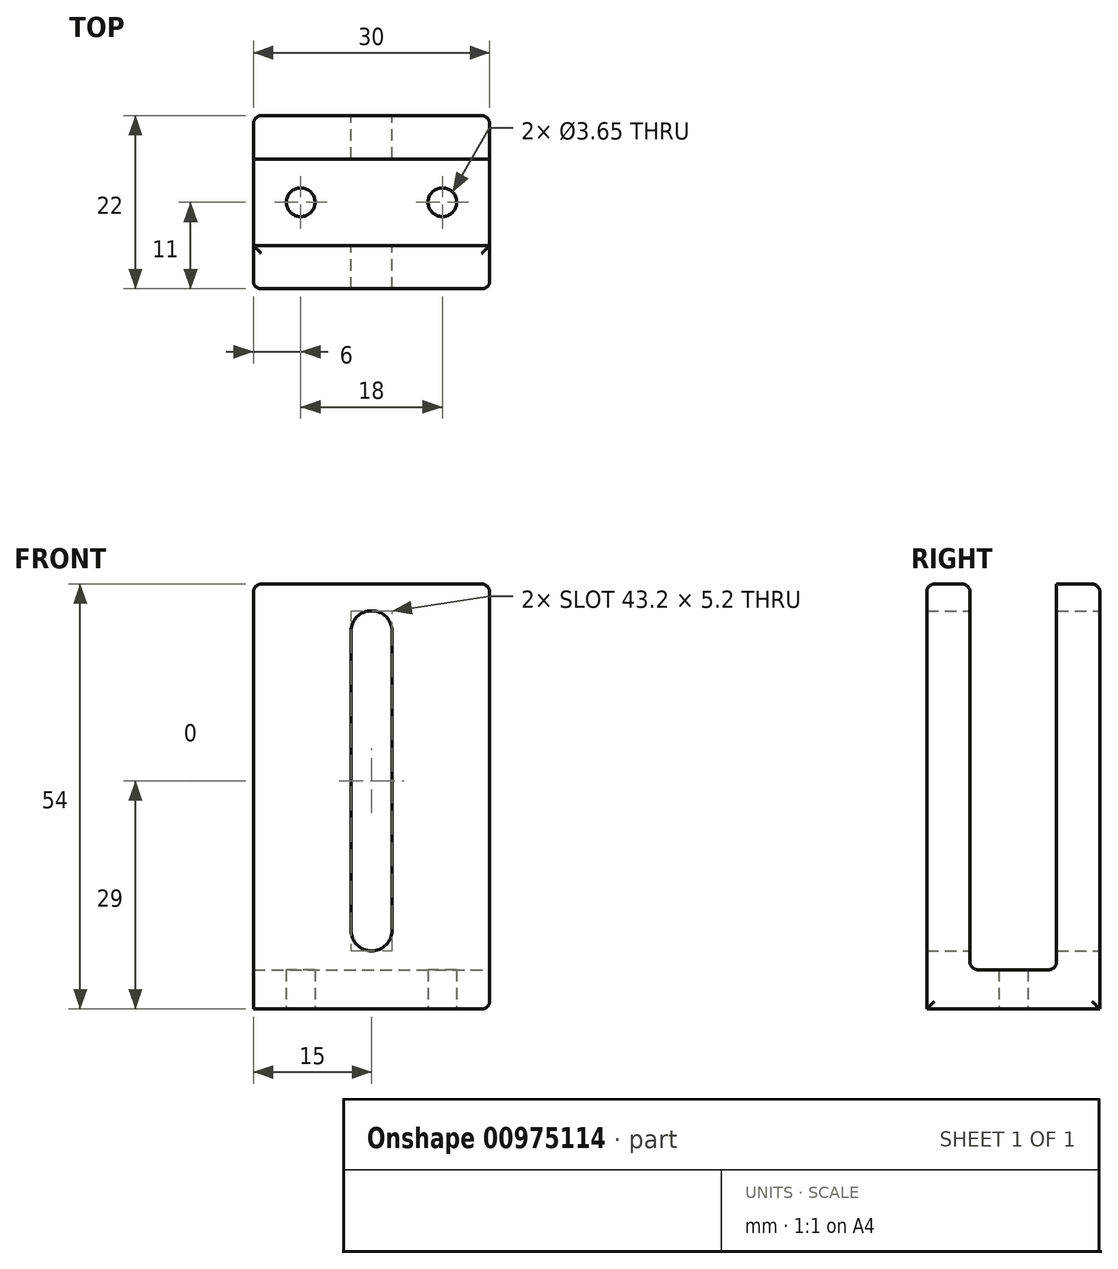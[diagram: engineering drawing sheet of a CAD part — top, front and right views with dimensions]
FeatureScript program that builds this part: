
annotation { "Feature Type Name" : "Feature", "Feature Type Description" : "" }
export const myFeature = defineFeature(function(context is Context, id is Id, definition is map)
    precondition{}
    {
        {
            var Q0;
            Q0=qCreatedBy(makeId("Front.planeOp"),FACE);
            var sketch = newSketch(context, id + "F0", { "sketchPlane" : qUnion([Q0])});
            skCircle(sketch, "E0", {"center": v(-15, 48) * mm, "radius": 2.5 * mm, "construction": true});
            skLineSegment(sketch, "E1.bottom", {"start": v(-30, 54) * mm, "end": v(0, 54) * mm});
            skLineSegment(sketch, "E1.top", {"start": v(-30, 0) * mm, "end": v(0, 0) * mm});
            skLineSegment(sketch, "E1.left", {"start": v(-30, 54) * mm, "end": v(-30, 0) * mm});
            skLineSegment(sketch, "E1.right", {"start": v(0, 54) * mm, "end": v(0, 0) * mm});
            skLineSegment(sketch, "E2", {"start": v(-15, 48) * mm, "end": v(-15, 10) * mm, "construction": true});
            skArc(sketch, "E3.0.startCap", {"start": v(-17.6, 48) * mm, "mid": v(-15, 50.6) * mm, "end": v(-12.4, 48) * mm});
            skArc(sketch, "E3.0.endCap", {"start": v(-12.4, 10) * mm, "mid": v(-15, 7.4) * mm, "end": v(-17.6, 10) * mm});
            skLineSegment(sketch, "E3.0.left", {"start": v(-12.4, 48) * mm, "end": v(-12.4, 10) * mm});
            skLineSegment(sketch, "E3.0.right", {"start": v(-17.6, 48) * mm, "end": v(-17.6, 10) * mm});
            skSolve(sketch);
        }
        {
            var Q0;
            Q0=makeQuery(id+"F0.imprint","IMPRINT",FACE,{"disambiguationData":[TD([[makeQuery(id+"F0.imprint","IMPRINT",EDGE,{"derivedFrom":sQuery(id+"F0.wireOp",EDGE,"E1.bottom")}),-1.0]])]});
            extrude(context, id + "F1", {"entities" : qUnion([Q0]), "endBound" : BoundingType.SYMMETRIC, "depth" : 22 * mm, "offsetDistance" : 25 * mm});
        }
        {
            var Q0;
            Q0=makeQuery(id+"F1.opExtrude","SWEPT_FACE",FACE,{"disambiguationData":[OSD([sQuery(id+"F0.wireOp",EDGE,"E1.bottom")])]});
            var sketch = newSketch(context, id + "F2", { "sketchPlane" : qUnion([Q0])});
            skLineSegment(sketch, "E4.bottom", {"start": v(0, 5.5) * mm, "end": v(-30, 5.5) * mm});
            skLineSegment(sketch, "E4.top", {"start": v(0, -5.5) * mm, "end": v(-30, -5.5) * mm});
            skLineSegment(sketch, "E4.left", {"start": v(0, 5.5) * mm, "end": v(0, -5.5) * mm});
            skLineSegment(sketch, "E4.right", {"start": v(-30, 5.5) * mm, "end": v(-30, -5.5) * mm});
            skLineSegment(sketch, "E5", {"start": v(13.11, 0) * mm, "end": v(-35.15, 0) * mm, "construction": true});
            skSolve(sketch);
        }
        {
            var Q0;
            Q0=makeQuery(id+"F2.imprint","IMPRINT",FACE,{"disambiguationData":[TD([[makeQuery(id+"F2.imprint","IMPRINT",EDGE,{"derivedFrom":sQuery(id+"F2.wireOp",EDGE,"E4.bottom")}),1.0]])]});
            var Q1;
            Q1=makeQuery(id+"F1.opExtrude","SWEPT_FACE",FACE,{"disambiguationData":[OSD([sQuery(id+"F0.wireOp",EDGE,"E1.top")])]});
            extrude(context, id + "F3", {"entities" : qUnion([Q0]), "operationType" : NewBodyOperationType.REMOVE, "endBound" : BoundingType.UP_TO_SURFACE, "oppositeDirection" : true, "depth" : 25 * mm, "endBoundEntityFace" : qUnion([Q1]), "hasOffset" : true, "offsetDistance" : 5 * mm});
        }
        {
            var Q0;
            Q0=qCreatedBy(makeId("Top.planeOp"),FACE);
            var sketch = newSketch(context, id + "F4", { "sketchPlane" : qUnion([Q0])});
            skCircle(sketch, "E6", {"center": v(-24, 0) * mm, "radius": 1.82 * mm});
            skLineSegment(sketch, "E7", {"start": v(-15, 11.1) * mm, "end": v(-15, -11.23) * mm, "construction": true});
            skCircle(sketch, "E8.MirrorC", {"center": v(-6, 0) * mm, "radius": 1.82 * mm});
            skSolve(sketch);
        }
        {
            var Q0;
            Q0 = qSketchRegion(id + "F4", true);
            var Q1;
            Q1=makeQuery(id+"F1.opExtrude","SWEPT_BODY",BODY,{"disambiguationData":[OSD([sQuery(id+"F0.wireOp",EDGE,"E1.bottom"),sQuery(id+"F0.wireOp",EDGE,"E1.top"),sQuery(id+"F0.wireOp",EDGE,"E1.left"),sQuery(id+"F0.wireOp",EDGE,"E1.right"),sQuery(id+"F0.wireOp",EDGE,"E3.0.startCap"),sQuery(id+"F0.wireOp",EDGE,"E3.0.endCap"),sQuery(id+"F0.wireOp",EDGE,"E3.0.left"),sQuery(id+"F0.wireOp",EDGE,"E3.0.right")])]});
            extrude(context, id + "F5", {"entities" : qUnion([Q0]), "operationType" : NewBodyOperationType.REMOVE, "endBound" : BoundingType.UP_TO_BODY, "depth" : 8 * mm, "endBoundEntityBody" : qUnion([Q1]), "offsetDistance" : 25 * mm});
        }
        {
            var Q0;
            Q0=makeQuery(id+"F3.boolean.opBoolean","COPY",EDGE,{"derivedFrom":makeQuery(id+"F3.opExtrude","CAP_EDGE",EDGE,{"disambiguationData":[OSD([sQuery(id+"F2.wireOp",EDGE,"E4.top")])],"isStart":false})});
            var Q1;
            Q1=makeQuery(id+"F3.boolean.opBoolean","COPY",EDGE,{"derivedFrom":makeQuery(id+"F3.opExtrude","CAP_EDGE",EDGE,{"disambiguationData":[OSD([sQuery(id+"F2.wireOp",EDGE,"E4.bottom")])],"isStart":false})});
            var Q2;
            Q2=makeQuery(id+"F1.opExtrude","CAP_EDGE",EDGE,{"disambiguationData":[OSD([sQuery(id+"F0.wireOp",EDGE,"E1.left")])],"isStart":false});
            var Q3;
            Q3=makeQuery(id+"F3.boolean.opBoolean","COPY",EDGE,{"derivedFrom":makeQuery(id+"F3.opExtrude","SWEPT_EDGE",EDGE,{"disambiguationData":[OSD([sQuery(id+"F0.wireOp",EDGE,"E1.bottom"),sQuery(id+"F0.wireOp",EDGE,"E1.left"),sQuery(id+"F2.wireOp",EDGE,"E4.top"),sQuery(id+"F2.wireOp",EDGE,"E4.right")])]})});
            var Q4;
            Q4=makeQuery(id+"F3.boolean.opBoolean","COPY",EDGE,{"derivedFrom":makeQuery(id+"F3.opExtrude","SWEPT_EDGE",EDGE,{"disambiguationData":[OSD([sQuery(id+"F0.wireOp",EDGE,"E1.bottom"),sQuery(id+"F0.wireOp",EDGE,"E1.left"),sQuery(id+"F2.wireOp",EDGE,"E4.bottom"),sQuery(id+"F2.wireOp",EDGE,"E4.right")])]})});
            var Q5;
            Q5=makeQuery(id+"F3.boolean.opBoolean","COPY",EDGE,{"derivedFrom":makeQuery(id+"F3.opExtrude","SWEPT_EDGE",EDGE,{"disambiguationData":[OSD([sQuery(id+"F0.wireOp",EDGE,"E1.bottom"),sQuery(id+"F0.wireOp",EDGE,"E1.right"),sQuery(id+"F2.wireOp",EDGE,"E4.bottom"),sQuery(id+"F2.wireOp",EDGE,"E4.left")])]})});
            var Q6;
            Q6=makeQuery(id+"F1.opExtrude","CAP_EDGE",EDGE,{"disambiguationData":[OSD([sQuery(id+"F0.wireOp",EDGE,"E1.right")])],"isStart":true});
            var Q7;
            Q7=makeQuery(id+"F1.opExtrude","CAP_EDGE",EDGE,{"disambiguationData":[OSD([sQuery(id+"F0.wireOp",EDGE,"E1.left")])],"isStart":true});
            var Q8;
            Q8=makeQuery(id+"F1.opExtrude","CAP_EDGE",EDGE,{"disambiguationData":[OSD([sQuery(id+"F0.wireOp",EDGE,"E1.bottom")])],"isStart":true});
            var Q9;
            Q9=makeQuery(id+"F3.boolean.opBoolean","COPY",EDGE,{"derivedFrom":makeQuery(id+"F3.opExtrude","CAP_EDGE",EDGE,{"disambiguationData":[OSD([sQuery(id+"F2.wireOp",EDGE,"E4.bottom")])],"isStart":true})});
            var Q10;
            Q10=makeQuery(id+"F1.opExtrude","CAP_EDGE",EDGE,{"disambiguationData":[OSD([sQuery(id+"F0.wireOp",EDGE,"E1.bottom")])],"isStart":false});
            var Q11;
            Q11=makeQuery(id+"F3.boolean.opBoolean","COPY",EDGE,{"derivedFrom":makeQuery(id+"F3.opExtrude","CAP_EDGE",EDGE,{"disambiguationData":[OSD([sQuery(id+"F2.wireOp",EDGE,"E4.top")])],"isStart":true})});
            var Q12;
            Q12=makeQuery(id+"F3.boolean.opBoolean","COPY",EDGE,{"derivedFrom":makeQuery(id+"F3.opExtrude","SWEPT_EDGE",EDGE,{"disambiguationData":[OSD([sQuery(id+"F0.wireOp",EDGE,"E1.bottom"),sQuery(id+"F0.wireOp",EDGE,"E1.right"),sQuery(id+"F2.wireOp",EDGE,"E4.top"),sQuery(id+"F2.wireOp",EDGE,"E4.left")])]})});
            var Q13;
            Q13=makeQuery(id+"F1.opExtrude","CAP_EDGE",EDGE,{"disambiguationData":[OSD([sQuery(id+"F0.wireOp",EDGE,"E1.right")])],"isStart":false});
            var Q14;
            {var subQ0=sQuery(id+"F0.wireOp",EDGE,"E1.bottom");var subQ1=sQuery(id+"F0.wireOp",EDGE,"E1.right");Q14=makeQuery(id+"F3.boolean.opBoolean","SPLIT",EDGE,{"disambiguationData":[TD([makeQuery(id+"F3.opExtrude","SWEPT_FACE",FACE,{"disambiguationData":[OSD([sQuery(id+"F2.wireOp",EDGE,"E4.top")])]})])],"derivedFrom":makeQuery(id+"F1.opExtrude","SWEPT_EDGE",EDGE,{"disambiguationData":[OSD([subQ0,subQ1])]})});}
            var Q15;
            {var subQ0=sQuery(id+"F0.wireOp",EDGE,"E1.bottom");var subQ1=sQuery(id+"F0.wireOp",EDGE,"E1.right");Q15=makeQuery(id+"F3.boolean.opBoolean","SPLIT",EDGE,{"disambiguationData":[TD([makeQuery(id+"F3.opExtrude","SWEPT_FACE",FACE,{"disambiguationData":[OSD([sQuery(id+"F2.wireOp",EDGE,"E4.bottom")])]})])],"derivedFrom":makeQuery(id+"F1.opExtrude","SWEPT_EDGE",EDGE,{"disambiguationData":[OSD([subQ0,subQ1])]})});}
            var Q16;
            Q16=makeQuery(id+"F1.opExtrude","SWEPT_EDGE",EDGE,{"disambiguationData":[OSD([sQuery(id+"F0.wireOp",EDGE,"E1.top"),sQuery(id+"F0.wireOp",EDGE,"E1.right")])]});
            var Q17;
            {var subQ0=sQuery(id+"F0.wireOp",EDGE,"E1.bottom");var subQ1=sQuery(id+"F0.wireOp",EDGE,"E1.left");Q17=makeQuery(id+"F3.boolean.opBoolean","SPLIT",EDGE,{"disambiguationData":[TD([makeQuery(id+"F3.opExtrude","SWEPT_FACE",FACE,{"disambiguationData":[OSD([sQuery(id+"F2.wireOp",EDGE,"E4.top")])]})])],"derivedFrom":makeQuery(id+"F1.opExtrude","SWEPT_EDGE",EDGE,{"disambiguationData":[OSD([subQ0,subQ1])]})});}
            var Q18;
            {var subQ0=sQuery(id+"F0.wireOp",EDGE,"E1.bottom");var subQ1=sQuery(id+"F0.wireOp",EDGE,"E1.left");Q18=makeQuery(id+"F3.boolean.opBoolean","SPLIT",EDGE,{"disambiguationData":[TD([makeQuery(id+"F3.opExtrude","SWEPT_FACE",FACE,{"disambiguationData":[OSD([sQuery(id+"F2.wireOp",EDGE,"E4.bottom")])]})])],"derivedFrom":makeQuery(id+"F1.opExtrude","SWEPT_EDGE",EDGE,{"disambiguationData":[OSD([subQ0,subQ1])]})});}
            fillet(context, id + "F6", {"entities" : qUnion([Q0, Q1, Q2, Q3, Q4, Q5, Q6, Q7, Q8, Q9, Q10, Q11, Q12, Q13, Q14, Q15, Q16, Q17, Q18]), "radius" : 1 * mm, "tangentPropagation" : true, "allowEdgeOverflow" : false});
        }
    });
